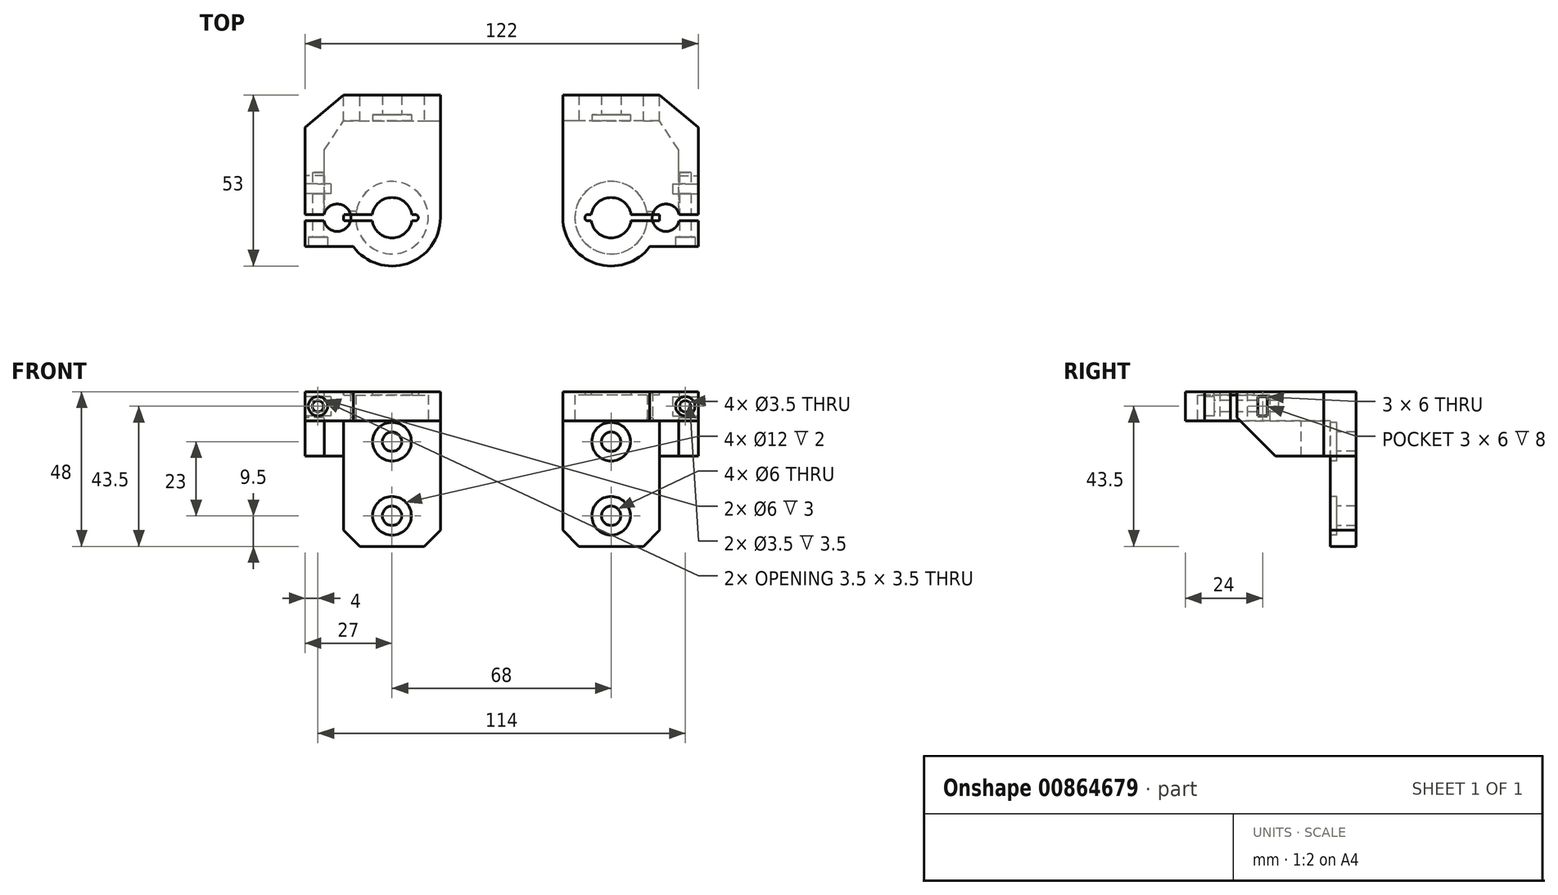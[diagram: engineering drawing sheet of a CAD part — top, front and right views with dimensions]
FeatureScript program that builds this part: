
annotation { "Feature Type Name" : "Feature", "Feature Type Description" : "" }
export const myFeature = defineFeature(function(context is Context, id is Id, definition is map)
    precondition{}
    {
        {
            var Q0;
            Q0=qCreatedBy(makeId("Front.planeOp"),FACE);
            var sketch = newSketch(context, id + "F0", { "sketchPlane" : qUnion([Q0])});
            skLineSegment(sketch, "E0.bottom", {"start": v(-15, 24) * mm, "end": v(15, 24) * mm});
            skLineSegment(sketch, "E0.top", {"start": v(-15, -24) * mm, "end": v(15, -24) * mm});
            skLineSegment(sketch, "E0.left", {"start": v(-15, 24) * mm, "end": v(-15, -24) * mm});
            skLineSegment(sketch, "E0.right", {"start": v(15, 24) * mm, "end": v(15, -24) * mm});
            skPoint(sketch, "E0.middle", {"position": v(0, 0) * mm});
            skSolve(sketch);
        }
        {
            var Q0;
            Q0=makeQuery(id+"F0.imprint","IMPRINT",FACE,{"disambiguationData":[TD([[makeQuery(id+"F0.imprint","IMPRINT",EDGE,{"derivedFrom":sQuery(id+"F0.wireOp",EDGE,"E0.bottom")}),-1.0]])]});
            extrude(context, id + "F1", {"entities" : qUnion([Q0]), "depth" : 8 * mm, "offsetDistance" : 25 * mm});
        }
        {
            var Q0;
            Q0=makeQuery(id+"F1.opExtrude","SWEPT_FACE",FACE,{"disambiguationData":[OSD([sQuery(id+"F0.wireOp",EDGE,"E0.bottom")])]});
            var sketch = newSketch(context, id + "F2", { "sketchPlane" : qUnion([Q0])});
            skLineSegment(sketch, "E1.bottom", {"start": v(15, 0) * mm, "end": v(-27, 0) * mm});
            skLineSegment(sketch, "E1.top", {"start": v(15, -53) * mm, "end": v(-27, -53) * mm});
            skLineSegment(sketch, "E1.left", {"start": v(15, 0) * mm, "end": v(15, -53) * mm});
            skLineSegment(sketch, "E1.right", {"start": v(-27, 0) * mm, "end": v(-27, -53) * mm});
            skLineSegment(sketch, "E2", {"start": v(-15, 0) * mm, "end": v(-27, -10) * mm});
            skLineSegment(sketch, "E3", {"start": v(15, -38) * mm, "end": v(-27, -38) * mm});
            skPoint(sketch, "E4.centerSnap0", {"position": v(0, -8) * mm});
            skLineSegment(sketch, "E5", {"start": v(-14.97, -37) * mm, "end": v(-27, -37) * mm});
            skLineSegment(sketch, "E6", {"start": v(-14.97, -39) * mm, "end": v(-27, -39) * mm});
            skArc(sketch, "E7", {"start": v(-14.97, -39) * mm, "mid": v(15, -38) * mm, "end": v(-14.97, -37) * mm});
            skLineSegment(sketch, "E8", {"start": v(-27, -47) * mm, "end": v(-12, -47) * mm});
            skCircle(sketch, "E9", {"center": v(0, -38) * mm, "radius": 15 * mm});
            skSolve(sketch);
        }
        {
            var Q0;
            {var subQ0=sQuery(id+"F2.wireOp",EDGE,"E2");Q0=makeQuery(id+"F2.imprint","IMPRINT",FACE,{"disambiguationData":[TD([[makeQuery(id+"F2.imprint","IMPRINT",EDGE,{"derivedFrom":subQ0}),1.0]])]});}
            var Q1;
            {var subQ3=sQuery(id+"F2.wireOp",EDGE,"Bgk35W4k-pg3z-gvu0-waTe-JFYPozHc3InJ");Q1=makeQuery(id+"F2.imprint","IMPRINT",FACE,{"disambiguationData":[TD([[makeQuery(id+"F2.imprint","IMPRINT",EDGE,{"derivedFrom":subQ3}),-1.0]])]});}
            var Q2;
            {var subQ0=sQuery(id+"F2.wireOp",EDGE,"E7");var subQ4=makeQuery(id+"F2.imprint","INTERSECT",VERTEX,{"derivedFrom":[sQuery(id+"F2.wireOp",EDGE,"E5"),subQ0]});Q2=makeQuery(id+"F2.imprint","IMPRINT",FACE,{"disambiguationData":[TD([[makeQuery(id+"F2.imprint","IMPRINT",EDGE,{"disambiguationData":[TD([[subQ4,-1.0]])],"derivedFrom":subQ0}),1.0]])]});}
            var Q3;
            {var subQ0=sQuery(id+"F2.wireOp",EDGE,"E7");var subQ3=makeQuery(id+"F2.imprint","INTERSECT",VERTEX,{"derivedFrom":[sQuery(id+"F2.wireOp",EDGE,"E6"),subQ0]});Q3=makeQuery(id+"F2.imprint","IMPRINT",FACE,{"disambiguationData":[TD([[makeQuery(id+"F2.imprint","IMPRINT",EDGE,{"disambiguationData":[TD([[subQ3,1.0]])],"derivedFrom":subQ0}),1.0]])]});}
            var Q4;
            {var subQ0=sQuery(id+"F2.wireOp",EDGE,"E6");Q4=makeQuery(id+"F2.imprint","IMPRINT",FACE,{"disambiguationData":[TD([[makeQuery(id+"F2.imprint","IMPRINT",EDGE,{"derivedFrom":subQ0}),1.0]])]});}
            var Q5;
            {var subQ0=sQuery(id+"F2.wireOp",EDGE,"E9");var subQ3=makeQuery(id+"F2.imprint","INTERSECT",VERTEX,{"derivedFrom":[sQuery(id+"F2.wireOp",EDGE,"E6"),subQ0]});Q5=makeQuery(id+"F2.imprint","IMPRINT",FACE,{"disambiguationData":[TD([[makeQuery(id+"F2.imprint","IMPRINT",EDGE,{"disambiguationData":[TD([[subQ3,1.0]])],"derivedFrom":subQ0}),1.0]])]});}
            var Q6;
            {var subQ0=sQuery(id+"F2.wireOp",EDGE,"E9");var subQ4=makeQuery(id+"F2.imprint","INTERSECT",VERTEX,{"derivedFrom":[sQuery(id+"F2.wireOp",EDGE,"E5"),subQ0]});Q6=makeQuery(id+"F2.imprint","IMPRINT",FACE,{"disambiguationData":[TD([[makeQuery(id+"F2.imprint","IMPRINT",EDGE,{"disambiguationData":[TD([[subQ4,-1.0]])],"derivedFrom":subQ0}),1.0]])]});}
            extrude(context, id + "F3", {"entities" : qUnion([Q0, Q1, Q2, Q3, Q4, Q5, Q6]), "operationType" : NewBodyOperationType.ADD, "oppositeDirection" : true, "depth" : 9 * mm, "offsetDistance" : 25 * mm});
        }
        {
            var Q0;
            Q0=makeQuery(id+"F3.opExtrude","CAP_FACE",FACE,{"disambiguationData":[OSD([sQuery(id+"F0.wireOp",EDGE,"E0.bottom"),sQuery(id+"F0.wireOp",EDGE,"E0.left"),sQuery(id+"F2.wireOp",EDGE,"E1.left"),sQuery(id+"F2.wireOp",EDGE,"E1.right"),sQuery(id+"F2.wireOp",EDGE,"E2"),sQuery(id+"F2.wireOp",EDGE,"E3"),sQuery(id+"F2.wireOp",EDGE,"oqEIAIsz-mzxT-sUn2-EQHF-xGBVEgtwxBgv"),sQuery(id+"F2.wireOp",EDGE,"Bgk35W4k-pg3z-gvu0-waTe-JFYPozHc3InJ"),sQuery(id+"F2.wireOp",EDGE,"E6")])],"isStart":false});
            var sketch = newSketch(context, id + "F4", { "sketchPlane" : qUnion([Q0])});
            skArc(sketch, "E10", {"start": v(-11.2, 37) * mm, "mid": v(11.25, 38) * mm, "end": v(-11.2, 39) * mm});
            skLineSegment(sketch, "E11", {"start": v(-14.97, 37) * mm, "end": v(-11.2, 37) * mm});
            skLineSegment(sketch, "E12", {"start": v(-14.97, 39) * mm, "end": v(-11.2, 39) * mm});
            skLineSegment(sketch, "E13", {"start": v(-14.97, 39) * mm, "end": v(-17, 39) * mm});
            skLineSegment(sketch, "E14", {"start": v(-17, 39) * mm, "end": v(-17, 37) * mm});
            skLineSegment(sketch, "E15", {"start": v(-17, 37) * mm, "end": v(-14.97, 37) * mm});
            skCircle(sketch, "E16", {"center": v(-17, 38) * mm, "radius": 4.25 * mm});
            skSolve(sketch);
        }
        {
            var Q0;
            Q0=makeQuery(id+"F4.imprint","IMPRINT",FACE,{"disambiguationData":[TD([[makeQuery(id+"F4.imprint","IMPRINT",EDGE,{"derivedFrom":sQuery(id+"F4.wireOp",EDGE,"E10")}),1.0]])]});
            var Q1;
            {var subQ0=sQuery(id+"F4.wireOp",EDGE,"E15");Q1=makeQuery(id+"F4.imprint","IMPRINT",FACE,{"disambiguationData":[TD([[makeQuery(id+"F4.imprint","IMPRINT",EDGE,{"derivedFrom":subQ0}),1.0]])]});}
            var Q2;
            {var subQ1=sQuery(id+"F2.wireOp",EDGE,"E9");var subQ3=makeQuery(id+"F3.opExtrude","CAP_EDGE",EDGE,{"disambiguationData":[OSD([subQ1]),TDD([makeQuery(id+"F2.imprint","IMPRINT",EDGE,{"disambiguationData":[TD([[makeQuery(id+"F2.imprint","INTERSECT",VERTEX,{"derivedFrom":[sQuery(id+"F2.wireOp",EDGE,"E5"),subQ1]}),-1.0]])],"derivedFrom":subQ1}),makeQuery(id+"F2.imprint","IMPRINT",EDGE,{"disambiguationData":[TD([[makeQuery(id+"F2.imprint","INTERSECT",VERTEX,{"derivedFrom":[sQuery(id+"F2.wireOp",EDGE,"E6"),subQ1]}),1.0]])],"derivedFrom":subQ1})])],"isStart":false});Q2=makeQuery(id+"F4.imprint","IMPRINT",FACE,{"disambiguationData":[TD([[makeQuery(id+"F4.imprint","IMPRINT",EDGE,{"derivedFrom":subQ3}),-1.0]])]});}
            var Q3;
            {var subQ0=sQuery(id+"F4.wireOp",EDGE,"E13");Q3=makeQuery(id+"F4.imprint","IMPRINT",FACE,{"disambiguationData":[TD([[makeQuery(id+"F4.imprint","IMPRINT",EDGE,{"derivedFrom":subQ0}),-1.0]])]});}
            extrude(context, id + "F5", {"entities" : qUnion([Q0, Q1, Q2, Q3]), "operationType" : NewBodyOperationType.REMOVE, "oppositeDirection" : true, "depth" : 8 * mm, "offsetDistance" : 25 * mm});
        }
        {
            var Q0;
            Q0=makeQuery(id+"F5.boolean.opBoolean","COPY",FACE,{"derivedFrom":makeQuery(id+"F5.opExtrude","CAP_FACE",FACE,{"disambiguationData":[OSD([sQuery(id+"F2.wireOp",EDGE,"E9"),sQuery(id+"F4.wireOp",EDGE,"E10"),sQuery(id+"F4.wireOp",EDGE,"E11"),sQuery(id+"F4.wireOp",EDGE,"E12")])],"isStart":false})});
            var sketch = newSketch(context, id + "F6", { "sketchPlane" : qUnion([Q0])});
            skCircle(sketch, "E17", {"center": v(0, 38) * mm, "radius": 6.25 * mm});
            skLineSegment(sketch, "E18", {"start": v(-16.07, 39) * mm, "end": v(-6.17, 39) * mm});
            skLineSegment(sketch, "E19", {"start": v(-16.07, 39) * mm, "end": v(-16.07, 37) * mm});
            skLineSegment(sketch, "E20", {"start": v(-16.07, 37) * mm, "end": v(-6.17, 37) * mm});
            skLineSegment(sketch, "E21", {"start": v(6.17, 39) * mm, "end": v(7.17, 39) * mm});
            skLineSegment(sketch, "E22", {"start": v(6.17, 37) * mm, "end": v(7.17, 37) * mm});
            skLineSegment(sketch, "E23", {"start": v(8.17, 38) * mm, "end": v(8.17, 38) * mm});
            skPoint(sketch, "E24.visualSharp", {"position": v(8.17, 39) * mm});
            skArc(sketch, "E24.filletArc", {"start": v(8.17, 38) * mm, "mid": v(7.88, 38.7) * mm, "end": v(7.17, 39) * mm});
            skPoint(sketch, "E25.visualSharp", {"position": v(8.17, 37) * mm});
            skArc(sketch, "E25.filletArc", {"start": v(7.17, 37) * mm, "mid": v(7.88, 37.3) * mm, "end": v(8.17, 38) * mm});
            skCircle(sketch, "E26", {"center": v(-17, 38) * mm, "radius": 4.25 * mm});
            skSolve(sketch);
        }
        {
            var Q0;
            {var subQ0=sQuery(id+"F6.wireOp",EDGE,"E17");var subQ1=makeQuery(id+"F6.imprint","INTERSECT",VERTEX,{"derivedFrom":[subQ0,sQuery(id+"F6.wireOp",EDGE,"E18")]});Q0=makeQuery(id+"F6.imprint","IMPRINT",FACE,{"disambiguationData":[TD([[makeQuery(id+"F6.imprint","IMPRINT",EDGE,{"disambiguationData":[TD([[subQ1,-1.0]])],"derivedFrom":subQ0}),1.0]])]});}
            var Q1;
            {var subQ1=makeQuery(id+"F5.boolean.opBoolean","COPY",EDGE,{"derivedFrom":makeQuery(id+"F5.opExtrude","CAP_EDGE",EDGE,{"disambiguationData":[OSD([sQuery(id+"F2.wireOp",EDGE,"E9")])],"isStart":false})});Q1=makeQuery(id+"F6.imprint","IMPRINT",FACE,{"disambiguationData":[TD([[makeQuery(id+"F6.imprint","IMPRINT",EDGE,{"derivedFrom":subQ1}),-1.0]])]});}
            var Q2;
            {var subQ2=sQuery(id+"F6.wireOp",EDGE,"E19");Q2=makeQuery(id+"F6.imprint","IMPRINT",FACE,{"disambiguationData":[TD([[makeQuery(id+"F6.imprint","IMPRINT",EDGE,{"derivedFrom":subQ2}),1.0]])]});}
            var Q3;
            {var subQ0=sQuery(id+"F6.wireOp",EDGE,"E21");Q3=makeQuery(id+"F6.imprint","IMPRINT",FACE,{"disambiguationData":[TD([[makeQuery(id+"F6.imprint","IMPRINT",EDGE,{"derivedFrom":subQ0}),-1.0]])]});}
            var Q4;
            {var subQ0=sQuery(id+"F6.wireOp",EDGE,"E20");var subQ4=sQuery(id+"F6.wireOp",EDGE,"E26");var subQ5=makeQuery(id+"F6.imprint","INTERSECT",VERTEX,{"derivedFrom":[subQ0,subQ4]});Q4=makeQuery(id+"F6.imprint","IMPRINT",FACE,{"disambiguationData":[TD([[makeQuery(id+"F6.imprint","IMPRINT",EDGE,{"disambiguationData":[TD([[subQ5,1.0]])],"derivedFrom":subQ0}),-1.0]])]});}
            var Q5;
            {var subQ0=sQuery(id+"F6.wireOp",EDGE,"E18");var subQ4=sQuery(id+"F6.wireOp",EDGE,"E26");var subQ5=makeQuery(id+"F6.imprint","INTERSECT",VERTEX,{"derivedFrom":[subQ0,subQ4]});Q5=makeQuery(id+"F6.imprint","IMPRINT",FACE,{"disambiguationData":[TD([[makeQuery(id+"F6.imprint","IMPRINT",EDGE,{"disambiguationData":[TD([[subQ5,1.0]])],"derivedFrom":subQ0}),1.0]])]});}
            var Q6;
            {var subQ0=sQuery(id+"F6.wireOp",EDGE,"E18");var subQ7=sQuery(id+"F6.wireOp",EDGE,"E17");var subQ9=makeQuery(id+"F6.imprint","INTERSECT",VERTEX,{"derivedFrom":[subQ7,subQ0]});Q6=makeQuery(id+"F6.imprint","IMPRINT",FACE,{"disambiguationData":[TD([[makeQuery(id+"F6.imprint","IMPRINT",EDGE,{"disambiguationData":[TD([[subQ9,-1.0]])],"derivedFrom":subQ7}),-1.0]])]});}
            extrude(context, id + "F7", {"entities" : qUnion([Q0, Q1, Q2, Q3, Q4, Q5, Q6]), "operationType" : NewBodyOperationType.REMOVE, "oppositeDirection" : true, "depth" : 1 * mm, "offsetDistance" : 25 * mm});
        }
        {
            var Q0;
            Q0=makeQuery(id+"F3.opExtrude","SWEPT_FACE",FACE,{"disambiguationData":[OSD([sQuery(id+"F2.wireOp",EDGE,"E8")])]});
            var sketch = newSketch(context, id + "F8", { "sketchPlane" : qUnion([Q0])});
            skCircle(sketch, "E27", {"center": v(-23, 19.5) * mm, "radius": 3 * mm});
            skPoint(sketch, "E27.centerSnap0", {"position": v(-27, 19.5) * mm});
            skSolve(sketch);
        }
        {
            var Q0;
            Q0=makeQuery(id+"F8.imprint","IMPRINT",FACE,{"disambiguationData":[TD([[makeQuery(id+"F8.imprint","IMPRINT",EDGE,{"derivedFrom":sQuery(id+"F8.wireOp",EDGE,"E27")}),1.0]])]});
            extrude(context, id + "F9", {"entities" : qUnion([Q0]), "operationType" : NewBodyOperationType.REMOVE, "oppositeDirection" : true, "depth" : 3 * mm, "offsetDistance" : 25 * mm});
        }
        {
            var Q0;
            Q0=makeQuery(id+"F9.boolean.opBoolean","COPY",FACE,{"derivedFrom":makeQuery(id+"F9.opExtrude","CAP_FACE",FACE,{"disambiguationData":[OSD([sQuery(id+"F8.wireOp",EDGE,"E27")])],"isStart":false})});
            var sketch = newSketch(context, id + "F10", { "sketchPlane" : qUnion([Q0])});
            skCircle(sketch, "E28", {"center": v(-23, 19.5) * mm, "radius": 1.75 * mm});
            skSolve(sketch);
        }
        {
            var Q0;
            Q0=makeQuery(id+"F10.imprint","IMPRINT",FACE,{"disambiguationData":[TD([[makeQuery(id+"F10.imprint","IMPRINT",EDGE,{"derivedFrom":sQuery(id+"F10.wireOp",EDGE,"E28")}),1.0]])]});
            extrude(context, id + "F11", {"entities" : qUnion([Q0]), "operationType" : NewBodyOperationType.REMOVE, "oppositeDirection" : true, "depth" : 20 * mm, "offsetDistance" : 25 * mm});
        }
        {
            var Q0;
            {var subQ0=sQuery(id+"F2.wireOp",EDGE,"E1.right");Q0=makeQuery(id+"F3.opExtrude","SWEPT_FACE",FACE,{"disambiguationData":[OSD([subQ0]),TDD([makeQuery(id+"F2.imprint","IMPRINT",EDGE,{"disambiguationData":[TD([[makeQuery(id+"F2.imprint","INTERSECT",VERTEX,{"derivedFrom":[subQ0,sQuery(id+"F2.wireOp",EDGE,"E2")]}),-1.0]])],"derivedFrom":subQ0})])]});}
            var sketch = newSketch(context, id + "F12", { "sketchPlane" : qUnion([Q0])});
            skLineSegment(sketch, "E29.bottom", {"start": v(27.5, 22.5) * mm, "end": v(30.5, 22.5) * mm});
            skLineSegment(sketch, "E29.top", {"start": v(27.5, 16.5) * mm, "end": v(30.5, 16.5) * mm});
            skLineSegment(sketch, "E29.left", {"start": v(27.5, 22.5) * mm, "end": v(27.5, 16.5) * mm});
            skLineSegment(sketch, "E29.right", {"start": v(30.5, 22.5) * mm, "end": v(30.5, 16.5) * mm});
            skPoint(sketch, "E29.middle", {"position": v(29, 19.5) * mm});
            skSolve(sketch);
        }
        {
            var Q0;
            Q0=makeQuery(id+"F12.imprint","IMPRINT",FACE,{"disambiguationData":[TD([[makeQuery(id+"F12.imprint","IMPRINT",EDGE,{"derivedFrom":sQuery(id+"F12.wireOp",EDGE,"E29.bottom")}),-1.0]])]});
            extrude(context, id + "F13", {"entities" : qUnion([Q0]), "operationType" : NewBodyOperationType.REMOVE, "oppositeDirection" : true, "depth" : 8 * mm, "offsetDistance" : 25 * mm});
        }
        {
            var Q0;
            Q0=makeQuery(id+"F3.opExtrude","CAP_FACE",FACE,{"disambiguationData":[OSD([sQuery(id+"F0.wireOp",EDGE,"E0.bottom"),sQuery(id+"F0.wireOp",EDGE,"E0.left"),sQuery(id+"F2.wireOp",EDGE,"E1.left"),sQuery(id+"F2.wireOp",EDGE,"E1.right"),sQuery(id+"F2.wireOp",EDGE,"E2"),sQuery(id+"F2.wireOp",EDGE,"E5"),sQuery(id+"F2.wireOp",EDGE,"E6"),sQuery(id+"F2.wireOp",EDGE,"E8"),sQuery(id+"F2.wireOp",EDGE,"E9")])],"isStart":false});
            var sketch = newSketch(context, id + "F14", { "sketchPlane" : qUnion([Q0])});
            skLineSegment(sketch, "E30", {"start": v(-27, 37) * mm, "end": v(-27, 10) * mm});
            skLineSegment(sketch, "E31", {"start": v(-27, 10) * mm, "end": v(-15, 0) * mm});
            skLineSegment(sketch, "E32", {"start": v(-15, 0) * mm, "end": v(-15, 8) * mm});
            skLineSegment(sketch, "E33", {"start": v(-27, 37) * mm, "end": v(-21, 37) * mm});
            skLineSegment(sketch, "E34", {"start": v(-21, 37) * mm, "end": v(-21, 17) * mm});
            skLineSegment(sketch, "E35", {"start": v(-21, 17) * mm, "end": v(-15, 8) * mm});
            skSolve(sketch);
        }
        {
            var Q0;
            Q0=makeQuery(id+"F14.imprint","IMPRINT",FACE,{"disambiguationData":[TD([[makeQuery(id+"F14.imprint","IMPRINT",EDGE,{"derivedFrom":sQuery(id+"F14.wireOp",EDGE,"E30")}),-1.0]])]});
            extrude(context, id + "F15", {"entities" : qUnion([Q0]), "operationType" : NewBodyOperationType.ADD, "depth" : 11 * mm, "offsetDistance" : 25 * mm});
        }
        {
            var Q0;
            {var subQ0=sQuery(id+"F2.wireOp",EDGE,"E1.right");Q0=makeQuery(id+"F15.boolean.opBoolean","MERGE",FACE,{"derivedFrom":[makeQuery(id+"F3.opExtrude","SWEPT_FACE",FACE,{"disambiguationData":[OSD([subQ0]),TDD([makeQuery(id+"F2.imprint","IMPRINT",EDGE,{"disambiguationData":[TD([[makeQuery(id+"F2.imprint","INTERSECT",VERTEX,{"derivedFrom":[subQ0,sQuery(id+"F2.wireOp",EDGE,"E2")]}),-1.0]])],"derivedFrom":subQ0})])]}),makeQuery(id+"F15.opExtrude","SWEPT_FACE",FACE,{"disambiguationData":[OSD([sQuery(id+"F14.wireOp",EDGE,"E30")])]})]});}
            var sketch = newSketch(context, id + "F16", { "sketchPlane" : qUnion([Q0])});
            skLineSegment(sketch, "E36", {"start": v(37, 16) * mm, "end": v(25, 4) * mm});
            skSolve(sketch);
        }
        {
            var Q0;
            {var subQ0=sQuery(id+"F16.wireOp",EDGE,"E36");Q0=makeQuery(id+"F16.imprint","IMPRINT",FACE,{"disambiguationData":[TD([[makeQuery(id+"F16.imprint","IMPRINT",EDGE,{"derivedFrom":subQ0}),1.0]])]});}
            extrude(context, id + "F17", {"entities" : qUnion([Q0]), "operationType" : NewBodyOperationType.REMOVE, "oppositeDirection" : true, "depth" : 25 * mm, "offsetDistance" : 25 * mm});
        }
        {
            var Q0;
            Q0=makeQuery(id+"F1.opExtrude","SWEPT_EDGE",EDGE,{"disambiguationData":[OSD([sQuery(id+"F0.wireOp",EDGE,"E0.top"),sQuery(id+"F0.wireOp",EDGE,"E0.left")])]});
            var Q1;
            Q1=makeQuery(id+"F1.opExtrude","SWEPT_EDGE",EDGE,{"disambiguationData":[OSD([sQuery(id+"F0.wireOp",EDGE,"E0.top"),sQuery(id+"F0.wireOp",EDGE,"E0.right")])]});
            chamfer(context, id + "F18", {"entities" : qUnion([Q0, Q1]), "width" : 5 * mm, "tangentPropagation" : true});
        }
        {
            var Q0;
            Q0=makeQuery(id+"F1.opExtrude","CAP_FACE",FACE,{"disambiguationData":[OSD([sQuery(id+"F0.wireOp",EDGE,"E0.bottom"),sQuery(id+"F0.wireOp",EDGE,"E0.top"),sQuery(id+"F0.wireOp",EDGE,"E0.left"),sQuery(id+"F0.wireOp",EDGE,"E0.right")])],"isStart":false});
            var sketch = newSketch(context, id + "F19", { "sketchPlane" : qUnion([Q0])});
            skCircle(sketch, "E37", {"center": v(0, 8.5) * mm, "radius": 6 * mm});
            skCircle(sketch, "E38.0.1.0", {"center": v(0, -14.5) * mm, "radius": 6 * mm});
            skLineSegment(sketch, "E38.direction1", {"start": v(0, 8.5) * mm, "end": v(25, 8.5) * mm, "construction": true});
            skLineSegment(sketch, "E38.direction2", {"start": v(0, 8.5) * mm, "end": v(0, -14.5) * mm, "construction": true});
            skSolve(sketch);
        }
        {
            var Q0;
            Q0=makeQuery(id+"F19.imprint","IMPRINT",FACE,{"disambiguationData":[TD([[makeQuery(id+"F19.imprint","IMPRINT",EDGE,{"derivedFrom":sQuery(id+"F19.wireOp",EDGE,"E37")}),1.0]])]});
            var Q1;
            Q1=makeQuery(id+"F19.imprint","IMPRINT",FACE,{"disambiguationData":[TD([[makeQuery(id+"F19.imprint","IMPRINT",EDGE,{"derivedFrom":sQuery(id+"F19.wireOp",EDGE,"E38.0.1.0")}),1.0]])]});
            extrude(context, id + "F20", {"entities" : qUnion([Q0, Q1]), "operationType" : NewBodyOperationType.REMOVE, "oppositeDirection" : true, "depth" : 2 * mm, "offsetDistance" : 25 * mm});
        }
        {
            var Q0;
            Q0=makeQuery(id+"F20.boolean.opBoolean","COPY",FACE,{"derivedFrom":makeQuery(id+"F20.opExtrude","CAP_FACE",FACE,{"disambiguationData":[OSD([sQuery(id+"F19.wireOp",EDGE,"E37")])],"isStart":false})});
            var sketch = newSketch(context, id + "F21", { "sketchPlane" : qUnion([Q0])});
            skCircle(sketch, "E39", {"center": v(0, 8.5) * mm, "radius": 3 * mm});
            skCircle(sketch, "E40.0.1.0", {"center": v(0, -14.5) * mm, "radius": 3 * mm});
            skLineSegment(sketch, "E40.direction1", {"start": v(0, 8.5) * mm, "end": v(25, 8.5) * mm, "construction": true});
            skLineSegment(sketch, "E40.direction2", {"start": v(0, 8.5) * mm, "end": v(0, -14.5) * mm, "construction": true});
            skSolve(sketch);
        }
        {
            var Q0;
            Q0=makeQuery(id+"F21.imprint","IMPRINT",FACE,{"disambiguationData":[TD([[makeQuery(id+"F21.imprint","IMPRINT",EDGE,{"derivedFrom":sQuery(id+"F21.wireOp",EDGE,"E39")}),1.0]])]});
            var Q1;
            Q1=makeQuery(id+"F21.imprint","IMPRINT",FACE,{"disambiguationData":[TD([[makeQuery(id+"F21.imprint","IMPRINT",EDGE,{"derivedFrom":sQuery(id+"F21.wireOp",EDGE,"E40.0.1.0")}),1.0]])]});
            extrude(context, id + "F22", {"entities" : qUnion([Q0, Q1]), "operationType" : NewBodyOperationType.REMOVE, "oppositeDirection" : true, "depth" : 25 * mm, "offsetDistance" : 25 * mm});
        }
        {
            var Q0;
            Q0=qCreatedBy(makeId("Right.planeOp"),FACE);
            cPlane(context, id + "F23", {"entities" : qUnion([Q0]), "cplaneType" : CPlaneType.OFFSET, "offset" : 34 * mm, "width" : 150 * mm, "height" : 150 * mm});
        }
        {
            var Q0;
            Q0=makeQuery(id+"F1.opExtrude","SWEPT_BODY",BODY,{"disambiguationData":[OSD([sQuery(id+"F0.wireOp",EDGE,"E0.bottom"),sQuery(id+"F0.wireOp",EDGE,"E0.top"),sQuery(id+"F0.wireOp",EDGE,"E0.left"),sQuery(id+"F0.wireOp",EDGE,"E0.right")])]});
            var Q1;
            Q1=qCreatedBy(id+"F23.planeOp",FACE);
            mirror(context, id + "F24", {"entities" : qUnion([Q0]), "mirrorPlane" : qUnion([Q1])});
        }
    });
